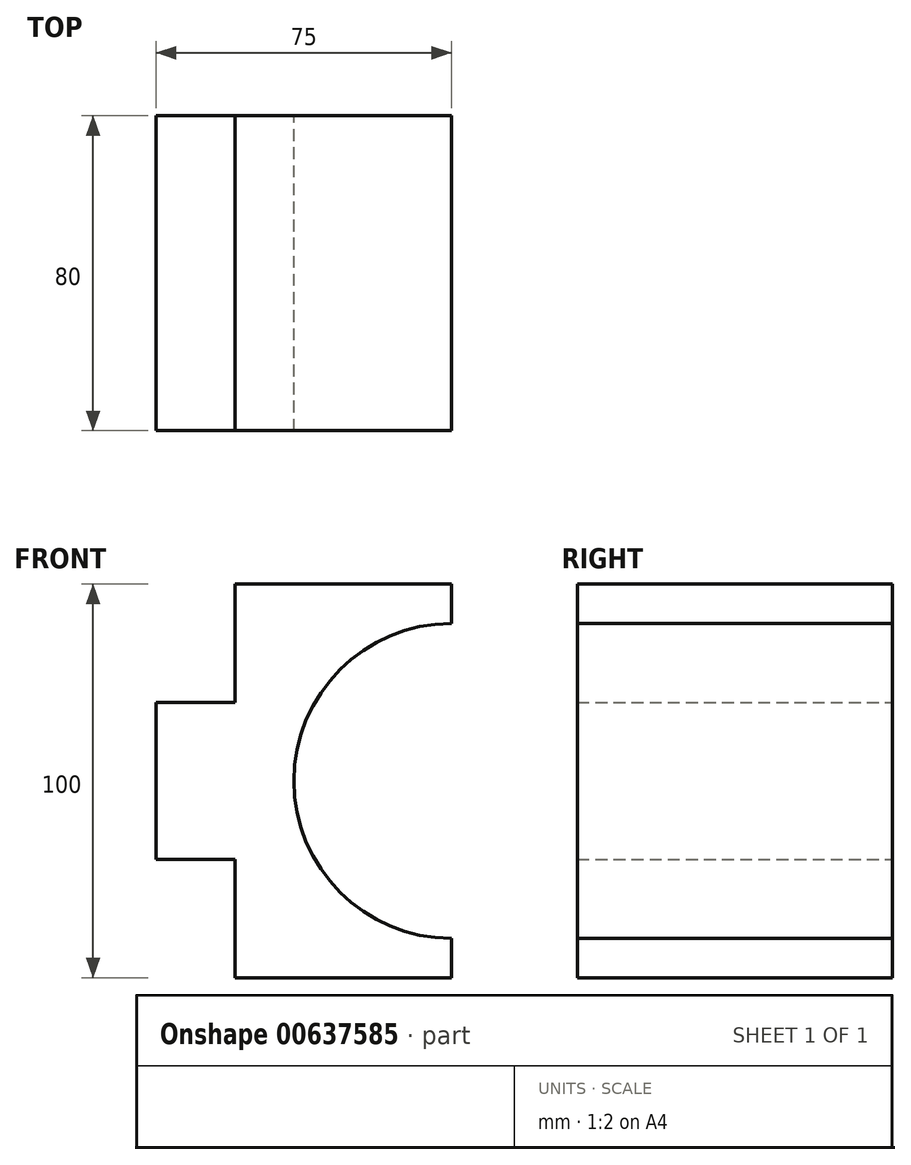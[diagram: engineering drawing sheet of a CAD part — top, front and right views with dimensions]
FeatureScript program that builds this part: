
annotation { "Feature Type Name" : "Feature", "Feature Type Description" : "" }
export const myFeature = defineFeature(function(context is Context, id is Id, definition is map)
    precondition{}
    {
        {
            var Q0;
            Q0=qCreatedBy(makeId("Front.planeOp"),FACE);
            var sketch = newSketch(context, id + "F0", { "sketchPlane" : qUnion([Q0])});
            skLineSegment(sketch, "E0", {"start": v(18.45, 46.83) * mm, "end": v(18.45, 36.83) * mm});
            skArc(sketch, "E1", {"start": v(18.45, 36.83) * mm, "mid": v(-21.55, -3.17) * mm, "end": v(18.45, -43.17) * mm});
            skLineSegment(sketch, "E2", {"start": v(18.45, 46.83) * mm, "end": v(-36.55, 46.83) * mm});
            skLineSegment(sketch, "E3", {"start": v(-36.55, -53.17) * mm, "end": v(18.45, -53.17) * mm});
            skLineSegment(sketch, "E4", {"start": v(-36.55, -53.17) * mm, "end": v(-36.55, -23.17) * mm});
            skLineSegment(sketch, "E5", {"start": v(-36.55, 46.83) * mm, "end": v(-36.55, 16.83) * mm});
            skLineSegment(sketch, "E6", {"start": v(-36.55, 16.83) * mm, "end": v(-56.55, 16.83) * mm});
            skLineSegment(sketch, "E7", {"start": v(-36.55, -23.17) * mm, "end": v(-56.55, -23.17) * mm});
            skLineSegment(sketch, "E8", {"start": v(-56.55, -23.17) * mm, "end": v(-56.55, 16.83) * mm});
            skLineSegment(sketch, "E9.trimOffspring", {"start": v(18.45, -43.17) * mm, "end": v(18.45, -53.17) * mm});
            skSolve(sketch);
        }
        {
            var Q0;
            Q0 = qSketchRegion(id + "F0", true);
            extrude(context, id + "F1", {"entities" : qUnion([Q0]), "depth" : 80 * mm, "offsetDistance" : 25 * mm});
        }
    });
